# Revit family: Genie_Site_ArticulatingBoom_Z60E1
name_source: partatom
category: Site
revit_build: Autodesk Revit 2017 (Build: 20160225_1515(x64)
units: mm (PartAtom-declared; Revit-internal decimal feet)

## family parameters
Always vertical = Yes
Cut with Voids When Loaded = No
OmniClass Number = 23.50.85.17.11
OmniClass Title = Electric and Battery Telescoping Platforms
Part Type = Normal
Round Connector Dimension = Use Diameter
Shared = No
Work Plane-Based = No

## types (1)
- Z60E
    Assembly Code = E1030900
    AssetType = Fixed
    BIMObjectName = Genie_Site_ArticulatingBoom_Z60E
    ClassificationName = Uniclass2015
    ClassificationValue = Pr_65_80_47_95
    Color = Grey & Blue
    Cost = 0 $
    Description = Powred by the latest generation of AC drive systems, thanks to its quiet, clean performance and powerful four-wheel drive abilities, the Genie® Z™-60 is a versatile, all-electric articulating boom lift, ideal for multiple outdoor and indoor tasks in the construction and facilities maintenance sectors. Examples range from sports arenas and malls to pedestrian areas were quiet, zero-emissions operation is required.
    DocumentationLiterature = https://www.genielift.com
    DocumentationTechnical = https://www.genielift.com
    DurationUnit = Years
    ExpectedLife = 0
    Features = The 5-ft (1.52 m) jib features a 135° range of motion to accurately position workers, Genie Fast Mast™ boom system allows operators to descend and retrieve materials and to quickly return to work at height, 4WD and full-time active oscillating axles provide traction for gradeability up to 45%, Proportional control system allows for quick, precise access to work areas for increased productivity
    Finish = Painted Steel
    IfcExportAs = IfcTransportElement
    IfcExportType = IfcTransportElementType
    Keynote = X
    Manufacturer = Genie
    ManufacturerName = Genie
    Material = Painted Steel
    Model = Genie - Articulating Boom
    ModelNumber = Z60E
    ModelReference = Genie - Articulating Boom
    NBSDescription = Vertical lifting platforms
    NBSObjectName = Genie - Vertical lifting platforms
    NBSReference = 90-80-65/350
    NominalDepth = 2490 mm
    NominalHeight = 2540 mm
    NominalLength = 8150 mm  [stored 26.7388 ft]
    ProductionYear = 2018
    ReplacementCost = 0
    Size = 2.49m x 2.54m x 8.15m
    Type Comments = Z60E
    TypeName = Genie - Articulating Boom
    URL = http://www.genielift.co.uk
    WarrantyDurationLabor = 0
    WarrantyDurationParts = 0
    WarrantyDurationUnit = Years
    WarrantyGuarantorLabor = http://www.genielift.co.uk
    WarrantyGuarantorParts = http://www.genielift.co.uk
    _BSBibleVersion = 15
    _BimSpecGuid = 0
    _CurrentRevision = 1
    _DistributedBy = www.bimstore.co.uk

note: [stored X ft] marks values corroborated as IEEE doubles in the binary element streams (Revit-internal decimal feet)

## geometry (parser evidence)
native form markers: Sweep x67
no freeform markers — native parametric forms only
